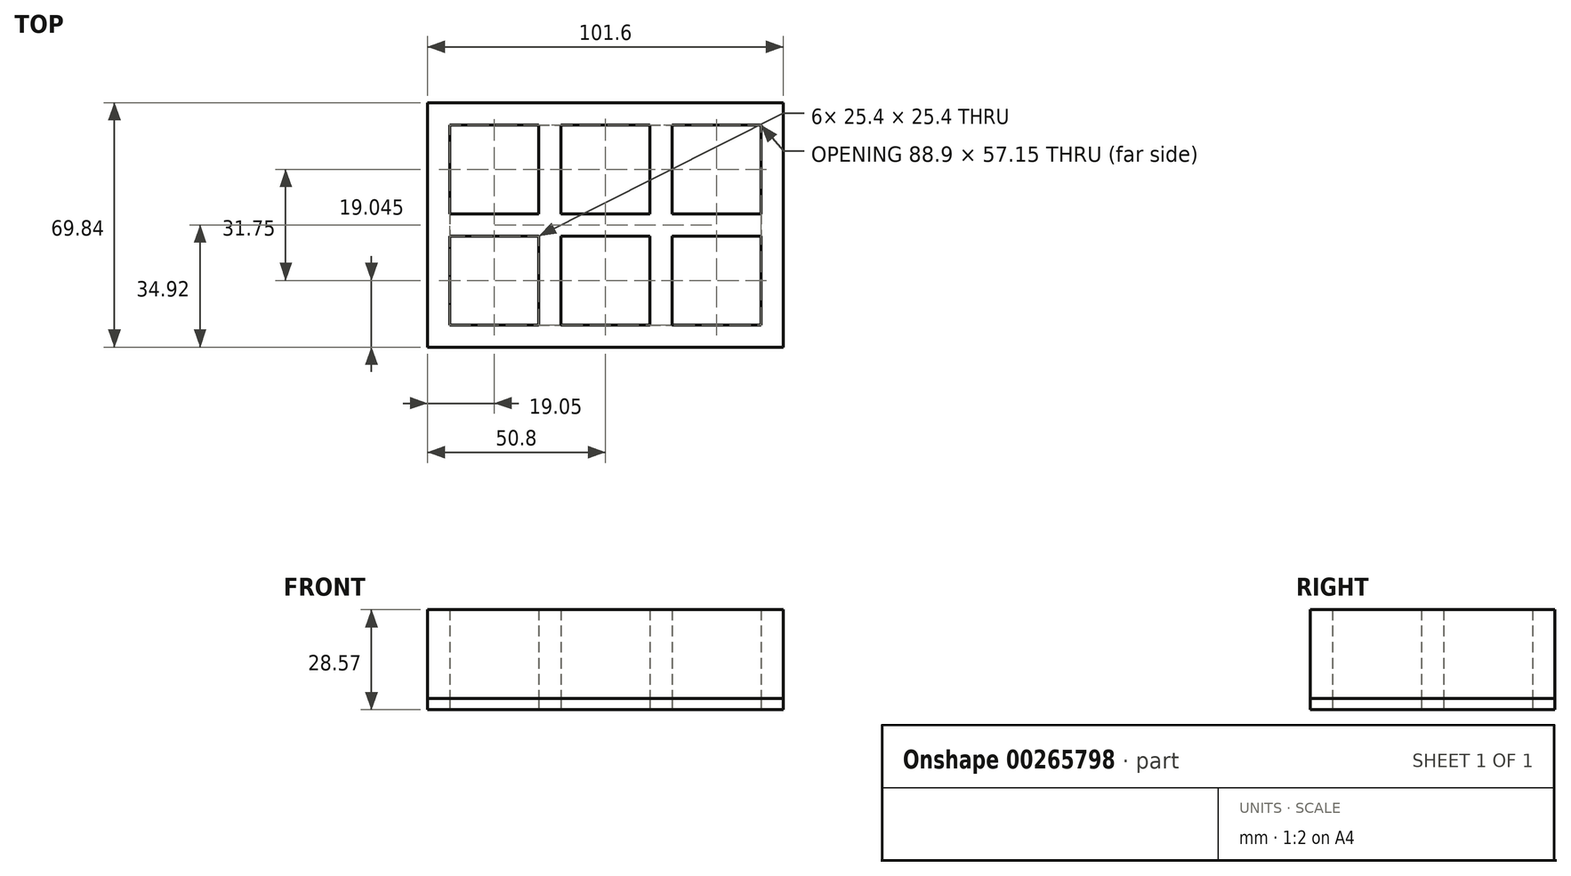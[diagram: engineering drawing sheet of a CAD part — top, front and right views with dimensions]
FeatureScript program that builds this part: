
annotation { "Feature Type Name" : "Feature", "Feature Type Description" : "" }
export const myFeature = defineFeature(function(context is Context, id is Id, definition is map)
    precondition{}
    {
        {
            var Q0;
            Q0=qCreatedBy(makeId("Top.planeOp"),FACE);
            var sketch = newSketch(context, id + "F0", { "sketchPlane" : qUnion([Q0])});
            skLineSegment(sketch, "E0.bottom", {"start": v(-50.8, 34.93) * mm, "end": v(50.8, 34.93) * mm});
            skLineSegment(sketch, "E0.top", {"start": v(-50.8, -34.93) * mm, "end": v(50.8, -34.93) * mm});
            skLineSegment(sketch, "E0.left", {"start": v(-50.8, 34.93) * mm, "end": v(-50.8, -34.93) * mm});
            skLineSegment(sketch, "E0.right", {"start": v(50.8, 34.93) * mm, "end": v(50.8, -34.93) * mm});
            skPoint(sketch, "E0.middle", {"position": v(0, 0) * mm});
            skLineSegment(sketch, "E1.bottom", {"start": v(-44.45, 28.57) * mm, "end": v(44.45, 28.57) * mm});
            skLineSegment(sketch, "E1.top", {"start": v(-44.45, -28.58) * mm, "end": v(44.45, -28.58) * mm});
            skLineSegment(sketch, "E1.left", {"start": v(-44.45, 28.57) * mm, "end": v(-44.45, -28.58) * mm});
            skLineSegment(sketch, "E1.right", {"start": v(44.45, 28.57) * mm, "end": v(44.45, -28.58) * mm});
            skLineSegment(sketch, "E2", {"start": v(-12.7, 28.57) * mm, "end": v(-12.7, -28.57) * mm});
            skLineSegment(sketch, "E3", {"start": v(19.05, -28.57) * mm, "end": v(19.05, 28.57) * mm});
            skLineSegment(sketch, "E4", {"start": v(12.7, 28.57) * mm, "end": v(12.7, -28.57) * mm});
            skLineSegment(sketch, "E5", {"start": v(-19.05, -28.57) * mm, "end": v(-19.05, 28.57) * mm});
            skLineSegment(sketch, "E6", {"start": v(-44.45, 3.17) * mm, "end": v(44.45, 3.17) * mm});
            skLineSegment(sketch, "E7", {"start": v(44.45, -3.18) * mm, "end": v(-44.45, -3.17) * mm});
            skSolve(sketch);
        }
        {
            var Q0;
            Q0 = qSketchRegion(id + "F0", true);
            var Q1;
            {var subQ0=sQuery(id+"F0.wireOp",EDGE,"E2");var subQ1=sQuery(id+"F0.wireOp",EDGE,"E1.bottom");var subQ2=makeQuery(id+"F0.imprint","INTERSECT",VERTEX,{"derivedFrom":[subQ1,subQ0]});Q1=makeQuery(id+"F0.imprint","IMPRINT",FACE,{"disambiguationData":[TD([[makeQuery(id+"F0.imprint","IMPRINT",EDGE,{"disambiguationData":[TD([[subQ2,1.0]])],"derivedFrom":subQ1}),-1.0]])]});}
            var Q2;
            {var subQ0=sQuery(id+"F0.wireOp",EDGE,"E6");var subQ1=sQuery(id+"F0.wireOp",EDGE,"E1.left");var subQ2=makeQuery(id+"F0.imprint","INTERSECT",VERTEX,{"derivedFrom":[subQ1,subQ0]});Q2=makeQuery(id+"F0.imprint","IMPRINT",FACE,{"disambiguationData":[TD([[makeQuery(id+"F0.imprint","IMPRINT",EDGE,{"disambiguationData":[TD([[subQ2,-1.0]])],"derivedFrom":subQ1}),1.0]])]});}
            var Q3;
            {var subQ0=sQuery(id+"F0.wireOp",EDGE,"E6");var subQ1=sQuery(id+"F0.wireOp",EDGE,"E2");var subQ2=makeQuery(id+"F0.imprint","INTERSECT",VERTEX,{"derivedFrom":[subQ1,subQ0]});Q3=makeQuery(id+"F0.imprint","IMPRINT",FACE,{"disambiguationData":[TD([[makeQuery(id+"F0.imprint","IMPRINT",EDGE,{"disambiguationData":[TD([[subQ2,-1.0]])],"derivedFrom":subQ1}),-1.0]])]});}
            var Q4;
            {var subQ0=sQuery(id+"F0.wireOp",EDGE,"E2");var subQ1=sQuery(id+"F0.wireOp",EDGE,"E1.top");var subQ2=makeQuery(id+"F0.imprint","INTERSECT",VERTEX,{"derivedFrom":[subQ1,subQ0]});Q4=makeQuery(id+"F0.imprint","IMPRINT",FACE,{"disambiguationData":[TD([[makeQuery(id+"F0.imprint","IMPRINT",EDGE,{"disambiguationData":[TD([[subQ2,1.0]])],"derivedFrom":subQ1}),1.0]])]});}
            var Q5;
            {var subQ0=sQuery(id+"F0.wireOp",EDGE,"E6");var subQ1=sQuery(id+"F0.wireOp",EDGE,"E2");var subQ2=makeQuery(id+"F0.imprint","INTERSECT",VERTEX,{"derivedFrom":[subQ1,subQ0]});Q5=makeQuery(id+"F0.imprint","IMPRINT",FACE,{"disambiguationData":[TD([[makeQuery(id+"F0.imprint","IMPRINT",EDGE,{"disambiguationData":[TD([[subQ2,-1.0]])],"derivedFrom":subQ1}),1.0]])]});}
            var Q6;
            {var subQ0=sQuery(id+"F0.wireOp",EDGE,"E3");var subQ1=sQuery(id+"F0.wireOp",EDGE,"E1.bottom");var subQ2=makeQuery(id+"F0.imprint","INTERSECT",VERTEX,{"derivedFrom":[subQ1,subQ0]});Q6=makeQuery(id+"F0.imprint","IMPRINT",FACE,{"disambiguationData":[TD([[makeQuery(id+"F0.imprint","IMPRINT",EDGE,{"disambiguationData":[TD([[subQ2,1.0]])],"derivedFrom":subQ1}),-1.0]])]});}
            var Q7;
            {var subQ0=sQuery(id+"F0.wireOp",EDGE,"E7");var subQ1=sQuery(id+"F0.wireOp",EDGE,"E3");var subQ2=makeQuery(id+"F0.imprint","INTERSECT",VERTEX,{"derivedFrom":[subQ1,subQ0]});Q7=makeQuery(id+"F0.imprint","IMPRINT",FACE,{"disambiguationData":[TD([[makeQuery(id+"F0.imprint","IMPRINT",EDGE,{"disambiguationData":[TD([[subQ2,-1.0]])],"derivedFrom":subQ1}),1.0]])]});}
            var Q8;
            {var subQ0=sQuery(id+"F0.wireOp",EDGE,"E6");var subQ1=sQuery(id+"F0.wireOp",EDGE,"E1.right");var subQ2=makeQuery(id+"F0.imprint","INTERSECT",VERTEX,{"derivedFrom":[subQ1,subQ0]});Q8=makeQuery(id+"F0.imprint","IMPRINT",FACE,{"disambiguationData":[TD([[makeQuery(id+"F0.imprint","IMPRINT",EDGE,{"disambiguationData":[TD([[subQ2,-1.0]])],"derivedFrom":subQ1}),-1.0]])]});}
            var Q9;
            {var subQ0=sQuery(id+"F0.wireOp",EDGE,"E3");var subQ1=sQuery(id+"F0.wireOp",EDGE,"E1.top");var subQ2=makeQuery(id+"F0.imprint","INTERSECT",VERTEX,{"derivedFrom":[subQ1,subQ0]});Q9=makeQuery(id+"F0.imprint","IMPRINT",FACE,{"disambiguationData":[TD([[makeQuery(id+"F0.imprint","IMPRINT",EDGE,{"disambiguationData":[TD([[subQ2,1.0]])],"derivedFrom":subQ1}),1.0]])]});}
            extrude(context, id + "F1", {"entities" : qUnion([Q0, Q1, Q2, Q3, Q4, Q5, Q6, Q7, Q8, Q9]), "depth" : 28.57 * mm});
        }
        {
            var Q0;
            {var subQ0=sQuery(id+"F0.wireOp",EDGE,"E1.left");var subQ1=sQuery(id+"F0.wireOp",EDGE,"E1.bottom");var subQ2=makeQuery(id+"F0.imprint","INTERSECT",VERTEX,{"derivedFrom":[subQ1,subQ0]});Q0=makeQuery(id+"F0.imprint","IMPRINT",FACE,{"disambiguationData":[TD([[makeQuery(id+"F0.imprint","IMPRINT",EDGE,{"disambiguationData":[TD([[subQ2,-1.0]])],"derivedFrom":subQ1}),-1.0]])]});}
            var Q1;
            {var subQ0=sQuery(id+"F0.wireOp",EDGE,"E2");var subQ1=sQuery(id+"F0.wireOp",EDGE,"E1.bottom");var subQ2=makeQuery(id+"F0.imprint","INTERSECT",VERTEX,{"derivedFrom":[subQ1,subQ0]});Q1=makeQuery(id+"F0.imprint","IMPRINT",FACE,{"disambiguationData":[TD([[makeQuery(id+"F0.imprint","IMPRINT",EDGE,{"disambiguationData":[TD([[subQ2,-1.0]])],"derivedFrom":subQ1}),-1.0]])]});}
            var Q2;
            {var subQ0=sQuery(id+"F0.wireOp",EDGE,"E1.left");var subQ1=sQuery(id+"F0.wireOp",EDGE,"E1.top");var subQ2=makeQuery(id+"F0.imprint","INTERSECT",VERTEX,{"derivedFrom":[subQ1,subQ0]});Q2=makeQuery(id+"F0.imprint","IMPRINT",FACE,{"disambiguationData":[TD([[makeQuery(id+"F0.imprint","IMPRINT",EDGE,{"disambiguationData":[TD([[subQ2,-1.0]])],"derivedFrom":subQ1}),1.0]])]});}
            var Q3;
            {var subQ0=sQuery(id+"F0.wireOp",EDGE,"E2");var subQ1=sQuery(id+"F0.wireOp",EDGE,"E1.top");var subQ2=makeQuery(id+"F0.imprint","INTERSECT",VERTEX,{"derivedFrom":[subQ1,subQ0]});Q3=makeQuery(id+"F0.imprint","IMPRINT",FACE,{"disambiguationData":[TD([[makeQuery(id+"F0.imprint","IMPRINT",EDGE,{"disambiguationData":[TD([[subQ2,-1.0]])],"derivedFrom":subQ1}),1.0]])]});}
            var Q4;
            {var subQ0=sQuery(id+"F0.wireOp",EDGE,"E1.right");var subQ1=sQuery(id+"F0.wireOp",EDGE,"E1.top");var subQ2=makeQuery(id+"F0.imprint","INTERSECT",VERTEX,{"derivedFrom":[subQ1,subQ0]});Q4=makeQuery(id+"F0.imprint","IMPRINT",FACE,{"disambiguationData":[TD([[makeQuery(id+"F0.imprint","IMPRINT",EDGE,{"disambiguationData":[TD([[subQ2,1.0]])],"derivedFrom":subQ1}),1.0]])]});}
            var Q5;
            {var subQ0=sQuery(id+"F0.wireOp",EDGE,"E1.right");var subQ1=sQuery(id+"F0.wireOp",EDGE,"E1.bottom");var subQ2=makeQuery(id+"F0.imprint","INTERSECT",VERTEX,{"derivedFrom":[subQ1,subQ0]});Q5=makeQuery(id+"F0.imprint","IMPRINT",FACE,{"disambiguationData":[TD([[makeQuery(id+"F0.imprint","IMPRINT",EDGE,{"disambiguationData":[TD([[subQ2,1.0]])],"derivedFrom":subQ1}),-1.0]])]});}
            var Q6;
            Q6=makeQuery(id+"F0.imprint","IMPRINT",FACE,{"disambiguationData":[TD([[makeQuery(id+"F0.imprint","IMPRINT",EDGE,{"derivedFrom":sQuery(id+"F0.wireOp",EDGE,"E0.bottom")}),-1.0]])]});
            extrude(context, id + "F2", {"entities" : qUnion([Q0, Q1, Q2, Q3, Q4, Q5, Q6]), "depth" : 3.17 * mm});
        }
    });
